# Revit family: 05-E146-Z5-CL
name_source: partatom
category: Luminarias
revit_build: Autodesk Revit 2017 (Build: 20160225_1515(x64)
units: mm (PartAtom-declared; Revit-internal decimal feet)

## family parameters
Anfitrión = Cara
Compartido = Sí
Corte con vacíos al cargar = No
Cota de conector redondo = Diámetro de uso
Número OmniClass = 23.80.70.00
Origen de luz = No
Punto de cálculo de habitación = No
Tipo de pieza = Normal
Título OmniClass = Lighting

## types (1)
- 05-E146-Z5-CL
    Acabado = Gris urbano, Arenado
    CRI = 80
    Carga aparente = 0 VA
    Catálogo = Outdoor
    CodigoGubimclass = 50.60.50.20
    CodigoOmniclass = 21-04 50 40
    CodigoUniclass2015 = EF_70_80
    CodigoUniformat2010 = D5040
    DescripcionGubimclass = Iluminación interior
    DescripcionOmniclass = Lighting
    DescripcionUniclass2015 = Lighting
    DescripcionUniformat2010 = Lighting
    EAN13 = 8435575319622
    Eficiencia energética = LED A++
    Elevación por defecto = 1000 mm  [stored 3.28084 ft]
    Etiqueta V/f = 220-240V/50-60Hz
    Fabricante = LEDS C4
    Familia = Tiny Short
    FechaVersion = Julio 2020
    Ficha = http://files.leds-c4.com
    Fotometría = http://files.leds-c4.com
    IK = IK10
    IMC = http://files.leds-c4.com
    IP = IP65
    IfcExportAs = IfcLightFixture
IfcLightFixture
    IfcExportType = NOTDEFINED
    Imagen web = http://files.leds-c4.com
    LDT = http://files.leds-c4.com
    Lumenes reales (lm) = 18
    Material = Aluminio, Cristal
    Peso neto (KG) = 0.53
    Producto descatalogado = Catalogado ES
    Rayo de luz = Check Photometric file
    Referencia = 05-E146-Z5-CL
    Temperatura color led (K) = Blanco cálido - 3000K
    Tender text (Castellano) = LEDS C4
Tiny Short
05-E146-Z5-CL

Empotrado de pared de uso exterior para iluminar frontalmente y hacia abajo. 
Metros cable incluido: 2. Material estructura: Aluminio. Acabado estructura: Gris urbano. Material difusor: Cristal. Acabado difusor: Arenado. Protección contra los rayos ultravioleta. Garantía: 5 Años. Ta max: 50ºC.

Peso neto del producto (Kg): 0.530
Longitud del producto (mm): 60
Anchura o diámetro del producto (mm): 82
Altura del producto (mm): 38
Salida del producto (mm): 2.5

Clase 1. IP: IP65. IK: IK10. LED. Nº de portalámparas o Leds: 16. Marca del LED: BRIDGELUX. Marca del Driver: HEP. Potencia máxima de la fuente de luz: 1.9W. Temperatura de color: Blanco cálido - 3000K. Índice de reproducción cromática: 80. Steps Mac Adam: 3. Diámetro máximo de la bombilla que admite la luminaria: 50.000h L80B20. UGR:  18.1. Riesgo fotobiológico: RG1. Flujo real (lm): 18. Lm/W reales: 6. Rango de voltaje/frecuencia: 220-240/50-60Hz. Voltaje: 3. Equipo incluido: Si, electrónico. Potencia total: 2.9. Factor de potencia: 0.50.
    Tender text (English) = LEDS C4
Tiny Short
05-E146-Z5-CL

Wall recessed for outdoor use. 

For frontal lighting and downlighting. Cable meters included: 2. Structure material: Aluminium. Structure finish: Urban grey. Diffuser material: Glass. Diffuser finish: Sandblasted. UV protection. Warranty: 5 Years. Ta max: 50ºC.

Product net weight (Kg): 0.530
Product length (mm): 60
Product width or diameter (mm): 82
Product height (mm): 38
Product aperture (mm): 2.5

Class 1. IP: IP65. IK: IK10. LED. No. of lampholders or LEDs: 16. LED brand: BRIDGELUX. Driver brand: HEP. Maximum power of light source: 1.9W. Colour temperature: LED warm-white 3000K. Colour rendering index: 80. MacAdam Steps: 3. Maximum diameter of luminaire bulb: 50.000h L80B20. UGR:  18.1. Photobiological risk: RG1. Real flux (lm): 18. Lm/Real W: 6. Voltage and frequency range: 220-240/50-60Hz. Voltage: 3. Gear included: Yes, electronic. Total power: 2.9. Power factor: 0.50.
    Tipo = Empotrable de pared
    Vatios (W) = 2.9
    Versión = v1

note: [stored X ft] marks values corroborated as IEEE doubles in the binary element streams (Revit-internal decimal feet)
